# Revit family: CMB-WM1016V-AA
name_source: partatom
category: Mechanical Equipment
revit_build: Autodesk Revit 2016 (Build: 20150220_1215(x64)
units: mm (PartAtom-declared; Revit-internal decimal feet)

## family parameters
Always vertical = Yes
Cut with Voids When Loaded = No
Host = Ceiling
OmniClass Number = 23.75.00.00
OmniClass Title = Climate Control (HVAC)
Part Type = Normal
Room Calculation Point = No
Round Connector Dimension = Use Radius
Shared = No

## types (60) — shared parameters
Connection pipe of indoor unit (Inlet Pipe)_radius (I.D.) = 10 mm  [stored 0.0328084 ft]
Connection pipe of indoor unit (Outlet Pipe)_radius (I.D.) = 10 mm  [stored 0.0328084 ft]
Depth = 630 mm  [stored 2.06693 ft]
Description = HBC controller
External Finish = Galvanized steel plate
Height = 300 mm  [stored 0.984252 ft]
Indoor unit capacity connectable to 1 branch = Model P80 or smaller (Use optional joint pipe combing 2 branches when the total unit capacity exceeds P81.)
Manufacturer = Mitsubishi Electric Corporation
Model = CMB-WM1016V-AA
Number of branch = 16
Phase = 1
Sound Pressure Level (dB(A)) = 41
Space View = Yes
Subcategory = HVAC
URL = http://www.mitsubishielectric.com
Unit Weight (kg) = 98
Width = 1800 mm  [stored 5.90551 ft]
zero-valued in all types: Equip_No., SerialNumber, TagNumber

## per-type parameters (varying)
| type | Connectable Outdoor/Heat source Unit | Connection pipe of outdoor/heat source unit (High pressure)_radius | Connection pipe of outdoor/heat source unit (Low pressure)_radius | Cooling Current (A) | Cooling Power Input (kW) | Heating Current (A) | Heating Power Input (kW) | Hertz | Voltage |
| CMB-WM1016V-AA_220V_50Hz_To M200 | PURY-M200YNW-A(-BS)/PURY-EM200YNW-A(-BS) | 8 mm  [stored 0.0262467 ft] | 10 mm  [stored 0.0328084 ft] | 2.89 | 0.45 | 2.89 | 0.45 | 50 Hz | 220 V |
| CMB-WM1016V-AA_220V_60Hz_To M200 | PURY-M200YNW-A(-BS)/PURY-EM200YNW-A(-BS) | 8 mm  [stored 0.0262467 ft] | 10 mm  [stored 0.0328084 ft] | 2.89 | 0.45 | 2.89 | 0.45 | 60 Hz | 220 V |
| CMB-WM1016V-AA_230V_50Hz_To M200 | PURY-M200YNW-A(-BS)/PURY-EM200YNW-A(-BS) | 8 mm  [stored 0.0262467 ft] | 10 mm  [stored 0.0328084 ft] | 2.83 | 0.46 | 2.83 | 0.46 | 50 Hz | 230 V |
| CMB-WM1016V-AA_230V_60Hz_To M200 | PURY-M200YNW-A(-BS)/PURY-EM200YNW-A(-BS) | 8 mm  [stored 0.0262467 ft] | 10 mm  [stored 0.0328084 ft] | 2.83 | 0.46 | 2.83 | 0.46 | 60 Hz | 230 V |
| CMB-WM1016V-AA_240V_50Hz_To M200 | PURY-M200YNW-A(-BS)/PURY-EM200YNW-A(-BS) | 8 mm  [stored 0.0262467 ft] | 10 mm  [stored 0.0328084 ft] | 2.79 | 0.47 | 2.79 | 0.47 | 50 Hz | 240 V |
| CMB-WM1016V-AA_240V_60Hz_To M200 | PURY-M200YNW-A(-BS)/PURY-EM200YNW-A(-BS) | 8 mm  [stored 0.0262467 ft] | 10 mm  [stored 0.0328084 ft] | 2.79 | 0.47 | 2.79 | 0.47 | 60 Hz | 240 V |
| CMB-WM1016V-AA_220V_50Hz_To M250 | PURY-M250YNW-A(-BS)/PURY-EM250YNW-A(-BS) | 8 mm  [stored 0.0262467 ft] | 10 mm  [stored 0.0328084 ft] | 2.89 | 0.45 | 2.89 | 0.45 | 50 Hz | 220 V |
| CMB-WM1016V-AA_220V_60Hz_To M250 | PURY-M250YNW-A(-BS)/PURY-EM250YNW-A(-BS) | 8 mm  [stored 0.0262467 ft] | 10 mm  [stored 0.0328084 ft] | 2.89 | 0.45 | 2.89 | 0.45 | 60 Hz | 220 V |
| CMB-WM1016V-AA_230V_50Hz_To M250 | PURY-M250YNW-A(-BS)/PURY-EM250YNW-A(-BS) | 8 mm  [stored 0.0262467 ft] | 10 mm  [stored 0.0328084 ft] | 2.83 | 0.46 | 2.83 | 0.46 | 50 Hz | 230 V |
| CMB-WM1016V-AA_230V_60Hz_To M250 | PURY-M250YNW-A(-BS)/PURY-EM250YNW-A(-BS) | 8 mm  [stored 0.0262467 ft] | 10 mm  [stored 0.0328084 ft] | 2.83 | 0.46 | 2.83 | 0.46 | 60 Hz | 230 V |
| CMB-WM1016V-AA_240V_50Hz_To M250 | PURY-M250YNW-A(-BS)/PURY-EM250YNW-A(-BS) | 8 mm  [stored 0.0262467 ft] | 10 mm  [stored 0.0328084 ft] | 2.79 | 0.47 | 2.79 | 0.47 | 50 Hz | 240 V |
| CMB-WM1016V-AA_240V_60Hz_To M250 | PURY-M250YNW-A(-BS)/PURY-EM250YNW-A(-BS) | 8 mm  [stored 0.0262467 ft] | 10 mm  [stored 0.0328084 ft] | 2.79 | 0.47 | 2.79 | 0.47 | 60 Hz | 240 V |
| CMB-WM1016V-AA_220V_50Hz_To M300 | PURY-M300YNW-A(-BS)/PURY-EM300YNW-A(-BS) | 8 mm  [stored 0.0262467 ft] | 10 mm  [stored 0.0328084 ft] | 2.89 | 0.45 | 2.89 | 0.45 | 50 Hz | 220 V |
| CMB-WM1016V-AA_220V_60Hz_To M300 | PURY-M300YNW-A(-BS)/PURY-EM300YNW-A(-BS) | 8 mm  [stored 0.0262467 ft] | 10 mm  [stored 0.0328084 ft] | 2.89 | 0.45 | 2.89 | 0.45 | 60 Hz | 220 V |
| CMB-WM1016V-AA_230V_50Hz_To M300 | PURY-M300YNW-A(-BS)/PURY-EM300YNW-A(-BS) | 8 mm  [stored 0.0262467 ft] | 10 mm  [stored 0.0328084 ft] | 2.83 | 0.46 | 2.83 | 0.46 | 50 Hz | 230 V |
| CMB-WM1016V-AA_230V_60Hz_To M300 | PURY-M300YNW-A(-BS)/PURY-EM300YNW-A(-BS) | 8 mm  [stored 0.0262467 ft] | 10 mm  [stored 0.0328084 ft] | 2.83 | 0.46 | 2.83 | 0.46 | 60 Hz | 230 V |
| CMB-WM1016V-AA_240V_50Hz_To M300 | PURY-M300YNW-A(-BS)/PURY-EM300YNW-A(-BS) | 8 mm  [stored 0.0262467 ft] | 10 mm  [stored 0.0328084 ft] | 2.79 | 0.47 | 2.79 | 0.47 | 50 Hz | 240 V |
| CMB-WM1016V-AA_240V_60Hz_To M300 | PURY-M300YNW-A(-BS)/PURY-EM300YNW-A(-BS) | 8 mm  [stored 0.0262467 ft] | 10 mm  [stored 0.0328084 ft] | 2.79 | 0.47 | 2.79 | 0.47 | 60 Hz | 240 V |
| CMB-WM1016V-AA_220V_50Hz_To P200 | PURY-P200YNW-A(-BS)/PURY-EP200YNW-A(-BS)/PURY-P200YLM-A(-BS)/PURY-P200YLM-A1(-BS)/PURY-EP200YLM-A1(-BS)/PQRY-P200YLM-A2/PQRY-P200YLM-A1 | 8 mm  [stored 0.0262467 ft] | 10 mm  [stored 0.0328084 ft] | 2.89 | 0.45 | 2.89 | 0.45 | 50 Hz | 220 V |
| CMB-WM1016V-AA_220V_60Hz_To P200 | PURY-P200YNW-A(-BS)/PURY-EP200YNW-A(-BS)/PURY-P200YLM-A(-BS)/PURY-P200YLM-A1(-BS)/PURY-EP200YLM-A1(-BS)/PQRY-P200YLM-A2/PQRY-P200YLM-A1 | 8 mm  [stored 0.0262467 ft] | 10 mm  [stored 0.0328084 ft] | 2.89 | 0.45 | 2.89 | 0.45 | 60 Hz | 220 V |
| CMB-WM1016V-AA_230V_50Hz_To P200 | PURY-P200YNW-A(-BS)/PURY-EP200YNW-A(-BS)/PURY-P200YLM-A(-BS)/PURY-P200YLM-A1(-BS)/PURY-EP200YLM-A1(-BS)/PQRY-P200YLM-A2/PQRY-P200YLM-A1 | 8 mm  [stored 0.0262467 ft] | 10 mm  [stored 0.0328084 ft] | 2.83 | 0.46 | 2.83 | 0.46 | 50 Hz | 230 V |
| CMB-WM1016V-AA_230V_60Hz_To P200 | PURY-P200YNW-A(-BS)/PURY-EP200YNW-A(-BS)/PURY-P200YLM-A(-BS)/PURY-P200YLM-A1(-BS)/PURY-EP200YLM-A1(-BS)/PQRY-P200YLM-A2/PQRY-P200YLM-A1 | 8 mm  [stored 0.0262467 ft] | 10 mm  [stored 0.0328084 ft] | 2.83 | 0.46 | 2.83 | 0.46 | 60 Hz | 230 V |
| CMB-WM1016V-AA_240V_50Hz_To P200 | PURY-P200YNW-A(-BS)/PURY-EP200YNW-A(-BS)/PURY-P200YLM-A(-BS)/PURY-P200YLM-A1(-BS)/PURY-EP200YLM-A1(-BS)/PQRY-P200YLM-A2/PQRY-P200YLM-A1 | 8 mm  [stored 0.0262467 ft] | 10 mm  [stored 0.0328084 ft] | 2.79 | 0.47 | 2.79 | 0.47 | 50 Hz | 240 V |
| CMB-WM1016V-AA_240V_60Hz_To P200 | PURY-P200YNW-A(-BS)/PURY-EP200YNW-A(-BS)/PURY-P200YLM-A(-BS)/PURY-P200YLM-A1(-BS)/PURY-EP200YLM-A1(-BS)/PQRY-P200YLM-A2/PQRY-P200YLM-A1 | 8 mm  [stored 0.0262467 ft] | 10 mm  [stored 0.0328084 ft] | 2.79 | 0.47 | 2.79 | 0.47 | 60 Hz | 240 V |
| CMB-WM1016V-AA_220V_50Hz_To P250 | PURY-P250YNW-A(-BS)/PURY-EP250YNW-A(-BS)/PURY-P250YLM-A(-BS)/PURY-P250YLM-A1(-BS)/PURY-EP250YLM-A1(-BS)/PQRY-P250YLM-A2/PQRY-P250YLM-A1 | 10 mm  [stored 0.0328084 ft] | 11 mm  [stored 0.0360892 ft] | 2.89 | 0.45 | 2.89 | 0.45 | 50 Hz | 220 V |
| CMB-WM1016V-AA_220V_60Hz_To P250 | PURY-P250YNW-A(-BS)/PURY-EP250YNW-A(-BS)/PURY-P250YLM-A(-BS)/PURY-P250YLM-A1(-BS)/PURY-EP250YLM-A1(-BS)/PQRY-P250YLM-A2/PQRY-P250YLM-A1 | 10 mm  [stored 0.0328084 ft] | 11 mm  [stored 0.0360892 ft] | 2.89 | 0.45 | 2.89 | 0.45 | 60 Hz | 220 V |
| CMB-WM1016V-AA_230V_50Hz_To P250 | PURY-P250YNW-A(-BS)/PURY-EP250YNW-A(-BS)/PURY-P250YLM-A(-BS)/PURY-P250YLM-A1(-BS)/PURY-EP250YLM-A1(-BS)/PQRY-P250YLM-A2/PQRY-P250YLM-A1 | 10 mm  [stored 0.0328084 ft] | 11 mm  [stored 0.0360892 ft] | 2.83 | 0.46 | 2.83 | 0.46 | 50 Hz | 230 V |
| CMB-WM1016V-AA_230V_60Hz_To P250 | PURY-P250YNW-A(-BS)/PURY-EP250YNW-A(-BS)/PURY-P250YLM-A(-BS)/PURY-P250YLM-A1(-BS)/PURY-EP250YLM-A1(-BS)/PQRY-P250YLM-A2/PQRY-P250YLM-A1 | 10 mm  [stored 0.0328084 ft] | 11 mm  [stored 0.0360892 ft] | 2.83 | 0.46 | 2.83 | 0.46 | 60 Hz | 230 V |
| CMB-WM1016V-AA_240V_50Hz_To P250 | PURY-P250YNW-A(-BS)/PURY-EP250YNW-A(-BS)/PURY-P250YLM-A(-BS)/PURY-P250YLM-A1(-BS)/PURY-EP250YLM-A1(-BS)/PQRY-P250YLM-A2/PQRY-P250YLM-A1 | 10 mm  [stored 0.0328084 ft] | 11 mm  [stored 0.0360892 ft] | 2.79 | 0.47 | 2.79 | 0.47 | 50 Hz | 240 V |
| CMB-WM1016V-AA_240V_60Hz_To P250 | PURY-P250YNW-A(-BS)/PURY-EP250YNW-A(-BS)/PURY-P250YLM-A(-BS)/PURY-P250YLM-A1(-BS)/PURY-EP250YLM-A1(-BS)/PQRY-P250YLM-A2/PQRY-P250YLM-A1 | 10 mm  [stored 0.0328084 ft] | 11 mm  [stored 0.0360892 ft] | 2.79 | 0.47 | 2.79 | 0.47 | 60 Hz | 240 V |
| CMB-WM1016V-AA_220V_50Hz_To P300 | PURY-P300YNW-A(-BS)/PURY-EP300YNW-A(-BS)/PURY-P300YLM-A(-BS)/PURY-P300YLM-A1(-BS)/PURY-EP300YLM-A1(-BS)/PQRY-P300YLM-A2/PQRY-P300YLM-A1 | 10 mm  [stored 0.0328084 ft] | 11 mm  [stored 0.0360892 ft] | 2.89 | 0.45 | 2.89 | 0.45 | 50 Hz | 220 V |
| CMB-WM1016V-AA_220V_60Hz_To P300 | PURY-P300YNW-A(-BS)/PURY-EP300YNW-A(-BS)/PURY-P300YLM-A(-BS)/PURY-P300YLM-A1(-BS)/PURY-EP300YLM-A1(-BS)/PQRY-P300YLM-A2/PQRY-P300YLM-A1 | 10 mm  [stored 0.0328084 ft] | 11 mm  [stored 0.0360892 ft] | 2.89 | 0.45 | 2.89 | 0.45 | 60 Hz | 220 V |
| CMB-WM1016V-AA_230V_50Hz_To P300 | PURY-P300YNW-A(-BS)/PURY-EP300YNW-A(-BS)/PURY-P300YLM-A(-BS)/PURY-P300YLM-A1(-BS)/PURY-EP300YLM-A1(-BS)/PQRY-P300YLM-A2/PQRY-P300YLM-A1 | 10 mm  [stored 0.0328084 ft] | 11 mm  [stored 0.0360892 ft] | 2.83 | 0.46 | 2.83 | 0.46 | 50 Hz | 230 V |
| CMB-WM1016V-AA_230V_60Hz_To P300 | PURY-P300YNW-A(-BS)/PURY-EP300YNW-A(-BS)/PURY-P300YLM-A(-BS)/PURY-P300YLM-A1(-BS)/PURY-EP300YLM-A1(-BS)/PQRY-P300YLM-A2/PQRY-P300YLM-A1 | 10 mm  [stored 0.0328084 ft] | 11 mm  [stored 0.0360892 ft] | 2.83 | 0.46 | 2.83 | 0.46 | 60 Hz | 230 V |
| CMB-WM1016V-AA_240V_50Hz_To P300 | PURY-P300YNW-A(-BS)/PURY-EP300YNW-A(-BS)/PURY-P300YLM-A(-BS)/PURY-P300YLM-A1(-BS)/PURY-EP300YLM-A1(-BS)/PQRY-P300YLM-A2/PQRY-P300YLM-A1 | 10 mm  [stored 0.0328084 ft] | 11 mm  [stored 0.0360892 ft] | 2.79 | 0.47 | 2.79 | 0.47 | 50 Hz | 240 V |
| CMB-WM1016V-AA_240V_60Hz_To P300 | PURY-P300YNW-A(-BS)/PURY-EP300YNW-A(-BS)/PURY-P300YLM-A(-BS)/PURY-P300YLM-A1(-BS)/PURY-EP300YLM-A1(-BS)/PQRY-P300YLM-A2/PQRY-P300YLM-A1 | 10 mm  [stored 0.0328084 ft] | 11 mm  [stored 0.0360892 ft] | 2.79 | 0.47 | 2.79 | 0.47 | 60 Hz | 240 V |
| CMB-WM1016V-AA_220V_50Hz_To P350 | PURY-P350YNW-A(-BS)/PURY-EP350YNW-A(-BS)/PURY-P350YLM-A(-BS)/PURY-P350YLM-A1(-BS)/PURY-EP350YLM-A1(-BS)/PQRY-P350YLM-A2/PQRY-P350YLM-A1 | 10 mm  [stored 0.0328084 ft] | 14 mm  [stored 0.0459318 ft] | 2.89 | 0.45 | 2.89 | 0.45 | 50 Hz | 220 V |
| CMB-WM1016V-AA_220V_60Hz_To P350 | PURY-P350YNW-A(-BS)/PURY-EP350YNW-A(-BS)/PURY-P350YLM-A(-BS)/PURY-P350YLM-A1(-BS)/PURY-EP350YLM-A1(-BS)/PQRY-P350YLM-A2/PQRY-P350YLM-A1 | 10 mm  [stored 0.0328084 ft] | 14 mm  [stored 0.0459318 ft] | 2.89 | 0.45 | 2.89 | 0.45 | 60 Hz | 220 V |
| CMB-WM1016V-AA_230V_50Hz_To P350 | PURY-P350YNW-A(-BS)/PURY-EP350YNW-A(-BS)/PURY-P350YLM-A(-BS)/PURY-P350YLM-A1(-BS)/PURY-EP350YLM-A1(-BS)/PQRY-P350YLM-A2/PQRY-P350YLM-A1 | 10 mm  [stored 0.0328084 ft] | 14 mm  [stored 0.0459318 ft] | 2.83 | 0.46 | 2.83 | 0.46 | 50 Hz | 230 V |
| CMB-WM1016V-AA_230V_60Hz_To P350 | PURY-P350YNW-A(-BS)/PURY-EP350YNW-A(-BS)/PURY-P350YLM-A(-BS)/PURY-P350YLM-A1(-BS)/PURY-EP350YLM-A1(-BS)/PQRY-P350YLM-A2/PQRY-P350YLM-A1 | 10 mm  [stored 0.0328084 ft] | 14 mm  [stored 0.0459318 ft] | 2.83 | 0.46 | 2.83 | 0.46 | 60 Hz | 230 V |
| CMB-WM1016V-AA_240V_50Hz_To P350 | PURY-P350YNW-A(-BS)/PURY-EP350YNW-A(-BS)/PURY-P350YLM-A(-BS)/PURY-P350YLM-A1(-BS)/PURY-EP350YLM-A1(-BS)/PQRY-P350YLM-A2/PQRY-P350YLM-A1 | 10 mm  [stored 0.0328084 ft] | 14 mm  [stored 0.0459318 ft] | 2.79 | 0.47 | 2.79 | 0.47 | 50 Hz | 240 V |
| CMB-WM1016V-AA_240V_60Hz_To P350 | PURY-P350YNW-A(-BS)/PURY-EP350YNW-A(-BS)/PURY-P350YLM-A(-BS)/PURY-P350YLM-A1(-BS)/PURY-EP350YLM-A1(-BS)/PQRY-P350YLM-A2/PQRY-P350YLM-A1 | 10 mm  [stored 0.0328084 ft] | 14 mm  [stored 0.0459318 ft] | 2.79 | 0.47 | 2.79 | 0.47 | 60 Hz | 240 V |
| CMB-WM1016V-AA_220V_50Hz_To P400 | PURY-P400YNW-A(-BS)/PURY-EP400YNW-A(-BS)/PURY-P400YLM-A(-BS)/PURY-P400YLM-A1(-BS)/PURY-EP400YLM-A1(-BS)/PQRY-P400YLM-A2/PQRY-P400YLM-A1 | 8 mm  [stored 0.0262467 ft] | 10 mm  [stored 0.0328084 ft] | 2.89 | 0.45 | 2.89 | 0.45 | 50 Hz | 220 V |
| CMB-WM1016V-AA_220V_60Hz_To P400 | PURY-P400YNW-A(-BS)/PURY-EP400YNW-A(-BS)/PURY-P400YLM-A(-BS)/PURY-P400YLM-A1(-BS)/PURY-EP400YLM-A1(-BS)/PQRY-P400YLM-A2/PQRY-P400YLM-A1 | 8 mm  [stored 0.0262467 ft] | 10 mm  [stored 0.0328084 ft] | 2.89 | 0.45 | 2.89 | 0.45 | 60 Hz | 220 V |
| CMB-WM1016V-AA_230V_50Hz_To P400 | PURY-P400YNW-A(-BS)/PURY-EP400YNW-A(-BS)/PURY-P400YLM-A(-BS)/PURY-P400YLM-A1(-BS)/PURY-EP400YLM-A1(-BS)/PQRY-P400YLM-A2/PQRY-P400YLM-A1 | 8 mm  [stored 0.0262467 ft] | 10 mm  [stored 0.0328084 ft] | 2.83 | 0.46 | 2.83 | 0.46 | 50 Hz | 230 V |
| CMB-WM1016V-AA_230V_60Hz_To P400 | PURY-P400YNW-A(-BS)/PURY-EP400YNW-A(-BS)/PURY-P400YLM-A(-BS)/PURY-P400YLM-A1(-BS)/PURY-EP400YLM-A1(-BS)/PQRY-P400YLM-A2/PQRY-P400YLM-A1 | 8 mm  [stored 0.0262467 ft] | 10 mm  [stored 0.0328084 ft] | 2.83 | 0.46 | 2.83 | 0.46 | 60 Hz | 230 V |
| CMB-WM1016V-AA_240V_50Hz_To P400 | PURY-P400YNW-A(-BS)/PURY-EP400YNW-A(-BS)/PURY-P400YLM-A(-BS)/PURY-P400YLM-A1(-BS)/PURY-EP400YLM-A1(-BS)/PQRY-P400YLM-A2/PQRY-P400YLM-A1 | 8 mm  [stored 0.0262467 ft] | 10 mm  [stored 0.0328084 ft] | 2.79 | 0.47 | 2.79 | 0.47 | 50 Hz | 240 V |
| CMB-WM1016V-AA_240V_60Hz_To P400 | PURY-P400YNW-A(-BS)/PURY-EP400YNW-A(-BS)/PURY-P400YLM-A(-BS)/PURY-P400YLM-A1(-BS)/PURY-EP400YLM-A1(-BS)/PQRY-P400YLM-A2/PQRY-P400YLM-A1 | 8 mm  [stored 0.0262467 ft] | 10 mm  [stored 0.0328084 ft] | 2.79 | 0.47 | 2.79 | 0.47 | 60 Hz | 240 V |
| CMB-WM1016V-AA_220V_50Hz_To P450 | PURY-P450YNW-A(-BS)/PURY-EP450YNW-A(-BS)/PURY-P450YLM-A(-BS)/PURY-P450YLM-A1(-BS)/PURY-EP450YLM-A1(-BS)/PQRY-P450YLM-A2/PQRY-P450YLM-A1 | 10 mm  [stored 0.0328084 ft] | 11 mm  [stored 0.0360892 ft] | 2.89 | 0.45 | 2.89 | 0.45 | 50 Hz | 220 V |
| CMB-WM1016V-AA_220V_60Hz_To P450 | PURY-P450YNW-A(-BS)/PURY-EP450YNW-A(-BS)/PURY-P450YLM-A(-BS)/PURY-P450YLM-A1(-BS)/PURY-EP450YLM-A1(-BS)/PQRY-P450YLM-A2/PQRY-P450YLM-A1 | 10 mm  [stored 0.0328084 ft] | 11 mm  [stored 0.0360892 ft] | 2.89 | 0.45 | 2.89 | 0.45 | 60 Hz | 220 V |
| CMB-WM1016V-AA_230V_50Hz_To P450 | PURY-P450YNW-A(-BS)/PURY-EP450YNW-A(-BS)/PURY-P450YLM-A(-BS)/PURY-P450YLM-A1(-BS)/PURY-EP450YLM-A1(-BS)/PQRY-P450YLM-A2/PQRY-P450YLM-A1 | 10 mm  [stored 0.0328084 ft] | 11 mm  [stored 0.0360892 ft] | 2.83 | 0.46 | 2.83 | 0.46 | 50 Hz | 230 V |
| CMB-WM1016V-AA_230V_60Hz_To P450 | PURY-P450YNW-A(-BS)/PURY-EP450YNW-A(-BS)/PURY-P450YLM-A(-BS)/PURY-P450YLM-A1(-BS)/PURY-EP450YLM-A1(-BS)/PQRY-P450YLM-A2/PQRY-P450YLM-A1 | 10 mm  [stored 0.0328084 ft] | 11 mm  [stored 0.0360892 ft] | 2.83 | 0.46 | 2.83 | 0.46 | 60 Hz | 230 V |
| CMB-WM1016V-AA_240V_50Hz_To P450 | PURY-P450YNW-A(-BS)/PURY-EP450YNW-A(-BS)/PURY-P450YLM-A(-BS)/PURY-P450YLM-A1(-BS)/PURY-EP450YLM-A1(-BS)/PQRY-P450YLM-A2/PQRY-P450YLM-A1 | 10 mm  [stored 0.0328084 ft] | 11 mm  [stored 0.0360892 ft] | 2.79 | 0.47 | 2.79 | 0.47 | 50 Hz | 240 V |
| CMB-WM1016V-AA_240V_60Hz_To P450 | PURY-P450YNW-A(-BS)/PURY-EP450YNW-A(-BS)/PURY-P450YLM-A(-BS)/PURY-P450YLM-A1(-BS)/PURY-EP450YLM-A1(-BS)/PQRY-P450YLM-A2/PQRY-P450YLM-A1 | 10 mm  [stored 0.0328084 ft] | 11 mm  [stored 0.0360892 ft] | 2.79 | 0.47 | 2.79 | 0.47 | 60 Hz | 240 V |
| CMB-WM1016V-AA_220V_50Hz_To P500 | PURY-P500YNW-A(-BS)/PURY-EP500YNW-A(-BS)/PURY-P500YLM-A(-BS)/PURY-P500YLM-A1(-BS)/PURY-EP500YLM-A1(-BS)/PQRY-P500YLM-A2/PQRY-P500YLM-A1 | 10 mm  [stored 0.0328084 ft] | 11 mm  [stored 0.0360892 ft] | 2.89 | 0.45 | 2.89 | 0.45 | 50 Hz | 220 V |
| CMB-WM1016V-AA_220V_60Hz_To P500 | PURY-P500YNW-A(-BS)/PURY-EP500YNW-A(-BS)/PURY-P500YLM-A(-BS)/PURY-P500YLM-A1(-BS)/PURY-EP500YLM-A1(-BS)/PQRY-P500YLM-A2/PQRY-P500YLM-A1 | 10 mm  [stored 0.0328084 ft] | 11 mm  [stored 0.0360892 ft] | 2.89 | 0.45 | 2.89 | 0.45 | 60 Hz | 220 V |
| CMB-WM1016V-AA_230V_50Hz_To P500 | PURY-P500YNW-A(-BS)/PURY-EP500YNW-A(-BS)/PURY-P500YLM-A(-BS)/PURY-P500YLM-A1(-BS)/PURY-EP500YLM-A1(-BS)/PQRY-P500YLM-A2/PQRY-P500YLM-A1 | 10 mm  [stored 0.0328084 ft] | 11 mm  [stored 0.0360892 ft] | 2.83 | 0.46 | 2.83 | 0.46 | 50 Hz | 230 V |
| CMB-WM1016V-AA_230V_60Hz_To P500 | PURY-P500YNW-A(-BS)/PURY-EP500YNW-A(-BS)/PURY-P500YLM-A(-BS)/PURY-P500YLM-A1(-BS)/PURY-EP500YLM-A1(-BS)/PQRY-P500YLM-A2/PQRY-P500YLM-A1 | 10 mm  [stored 0.0328084 ft] | 11 mm  [stored 0.0360892 ft] | 2.83 | 0.46 | 2.83 | 0.46 | 60 Hz | 230 V |
| CMB-WM1016V-AA_240V_50Hz_To P500 | PURY-P500YNW-A(-BS)/PURY-EP500YNW-A(-BS)/PURY-P500YLM-A(-BS)/PURY-P500YLM-A1(-BS)/PURY-EP500YLM-A1(-BS)/PQRY-P500YLM-A2/PQRY-P500YLM-A1 | 10 mm  [stored 0.0328084 ft] | 11 mm  [stored 0.0360892 ft] | 2.79 | 0.47 | 2.79 | 0.47 | 50 Hz | 240 V |
| CMB-WM1016V-AA_240V_60Hz_To P500 | PURY-P500YNW-A(-BS)/PURY-EP500YNW-A(-BS)/PURY-P500YLM-A(-BS)/PURY-P500YLM-A1(-BS)/PURY-EP500YLM-A1(-BS)/PQRY-P500YLM-A2/PQRY-P500YLM-A1 | 10 mm  [stored 0.0328084 ft] | 11 mm  [stored 0.0360892 ft] | 2.79 | 0.47 | 2.79 | 0.47 | 60 Hz | 240 V |

note: [stored X ft] marks values corroborated as IEEE doubles in the binary element streams (Revit-internal decimal feet)

## geometry (parser evidence)
native form markers: Blend x80, Sweep x16
no freeform markers — native parametric forms only
